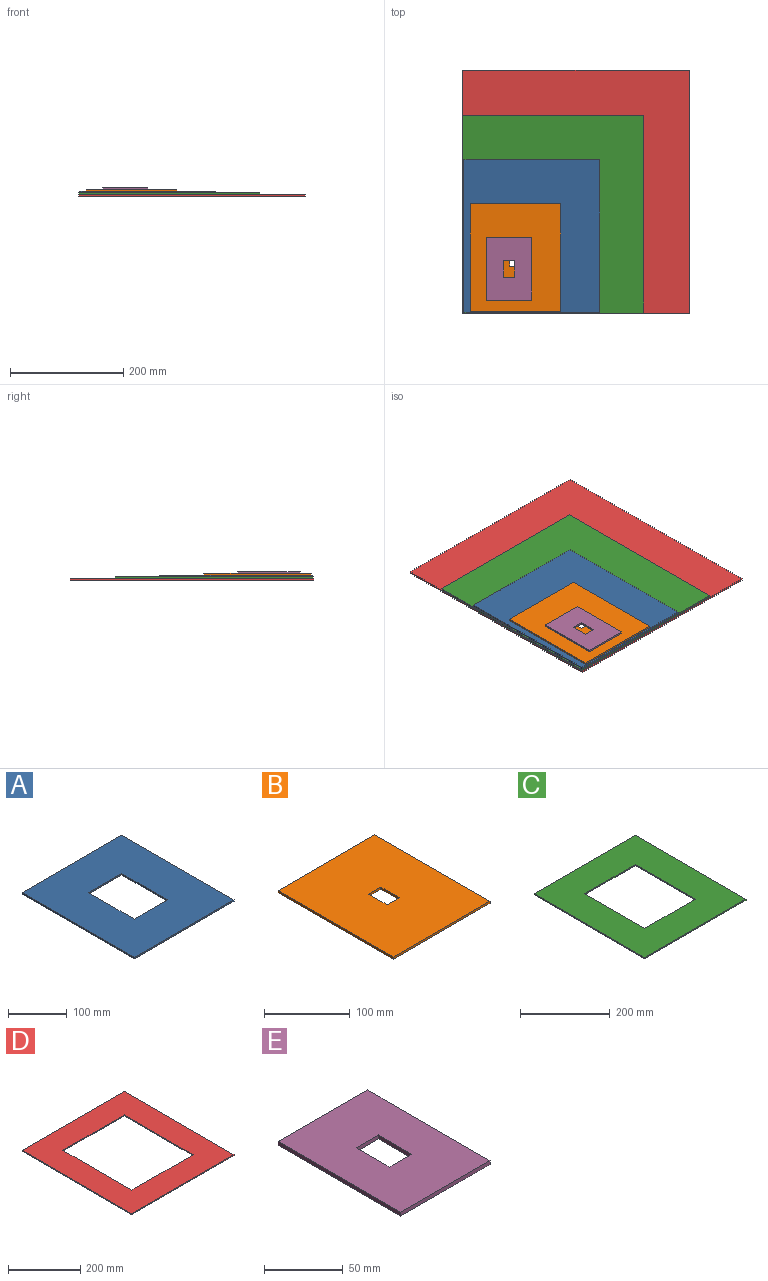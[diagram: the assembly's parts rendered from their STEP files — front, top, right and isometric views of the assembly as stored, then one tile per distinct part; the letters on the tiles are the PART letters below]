
ASSEMBLY  parts=5 mates=4
PART A: 10 faces, bbox 240x270x3 mm
  f0: plane 110x3mm, normal (1,0,0), area 330mm2, adj f1,f7,f8,f9
  f1: plane 80x3mm, normal (0,-1,0), area 240mm2, adj f0,f2,f8,f9
  f2: plane 110x3mm, normal (-1,0,0), area 330mm2, adj f1,f7,f8,f9
  f3: plane 270x3mm, normal (-1,0,0), area 810mm2, adj f4,f6,f8,f9
  f4: plane 240x3mm, normal (0,-1,0), area 720mm2, adj f3,f5,f8,f9
  f5: plane 270x3mm, normal (1,0,0), area 810mm2, adj f4,f6,f8,f9
  f6: plane 240x3mm, normal (0,1,0), area 720mm2, adj f3,f5,f8,f9
  f7: plane 80x3mm, normal (0,1,0), area 240mm2, adj f0,f2,f8,f9
  f8: plane 270x240mm, normal (0,0,1), area 56000mm2, adj f0,f1,f2,f3,f4,f5,f6,f7
  f9: plane 270x240mm, normal (0,0,-1), area 56000mm2, adj f0,f1,f2,f3,f4,f5,f6,f7
PART B: 10 faces, bbox 160x190x3 mm
  f0: plane 30x3mm, normal (1,0,0), area 90mm2, adj f1,f7,f8,f9
  f1: plane 20x3mm, normal (0,-1,0), area 60mm2, adj f0,f2,f8,f9
  f2: plane 30x3mm, normal (-1,0,0), area 90mm2, adj f1,f7,f8,f9
  f3: plane 160x3mm, normal (0,1,0), area 480mm2, adj f4,f6,f8,f9
  f4: plane 190x3mm, normal (-1,0,0), area 570mm2, adj f3,f5,f8,f9
  f5: plane 160x3mm, normal (0,-1,0), area 480mm2, adj f4,f6,f8,f9
  f6: plane 190x3mm, normal (1,0,0), area 570mm2, adj f3,f5,f8,f9
  f7: plane 20x3mm, normal (0,1,0), area 60mm2, adj f0,f2,f8,f9
  f8: plane 190x160mm, normal (0,0,1), area 29800mm2, adj f0,f1,f2,f3,f4,f5,f6,f7
  f9: plane 190x160mm, normal (0,0,-1), area 29800mm2, adj f0,f1,f2,f3,f4,f5,f6,f7
PART C: 10 faces, bbox 320x350x3 mm
  f0: plane 190x3mm, normal (1,0,0), area 570mm2, adj f1,f7,f8,f9
  f1: plane 160x3mm, normal (0,-1,0), area 480mm2, adj f0,f2,f8,f9
  f2: plane 190x3mm, normal (-1,0,0), area 570mm2, adj f1,f7,f8,f9
  f3: plane 350x3mm, normal (-1,0,0), area 1050mm2, adj f4,f6,f8,f9
  f4: plane 320x3mm, normal (0,-1,0), area 960mm2, adj f3,f5,f8,f9
  f5: plane 350x3mm, normal (1,0,0), area 1050mm2, adj f4,f6,f8,f9
  f6: plane 320x3mm, normal (0,1,0), area 960mm2, adj f3,f5,f8,f9
  f7: plane 160x3mm, normal (0,1,0), area 480mm2, adj f0,f2,f8,f9
  f8: plane 350x320mm, normal (0,0,1), area 81600mm2, adj f0,f1,f2,f3,f4,f5,f6,f7
  f9: plane 350x320mm, normal (0,0,-1), area 81600mm2, adj f0,f1,f2,f3,f4,f5,f6,f7
PART D: 10 faces, bbox 400x430x3 mm
  f0: plane 270x3mm, normal (-1,0,0), area 810mm2, adj f1,f7,f8,f9
  f1: plane 240x3mm, normal (0,1,0), area 720mm2, adj f0,f2,f8,f9
  f2: plane 270x3mm, normal (1,0,0), area 810mm2, adj f1,f7,f8,f9
  f3: plane 400x3mm, normal (0,1,0), area 1200mm2, adj f4,f6,f8,f9
  f4: plane 430x3mm, normal (-1,0,0), area 1290mm2, adj f3,f5,f8,f9
  f5: plane 400x3mm, normal (0,-1,0), area 1200mm2, adj f4,f6,f8,f9
  f6: plane 430x3mm, normal (1,0,0), area 1290mm2, adj f3,f5,f8,f9
  f7: plane 240x3mm, normal (0,-1,0), area 720mm2, adj f0,f2,f8,f9
  f8: plane 430x400mm, normal (0,0,1), area 107200mm2, adj f0,f1,f2,f3,f4,f5,f6,f7
  f9: plane 430x400mm, normal (0,0,-1), area 107200mm2, adj f0,f1,f2,f3,f4,f5,f6,f7
PART E: 10 faces, bbox 80x110x3 mm
  f0: plane 80x3mm, normal (0,1,0), area 240mm2, adj f1,f7,f8,f9
  f1: plane 110x3mm, normal (-1,0,0), area 330mm2, adj f0,f2,f8,f9
  f2: plane 80x3mm, normal (0,-1,0), area 240mm2, adj f1,f7,f8,f9
  f3: plane 30x3mm, normal (1,0,0), area 90mm2, adj f4,f6,f8,f9
  f4: plane 20x3mm, normal (0,-1,0), area 60mm2, adj f3,f5,f8,f9
  f5: plane 30x3mm, normal (-1,0,0), area 90mm2, adj f4,f6,f8,f9
  f6: plane 20x3mm, normal (0,1,0), area 60mm2, adj f3,f5,f8,f9
  f7: plane 110x3mm, normal (1,0,0), area 330mm2, adj f0,f2,f8,f9
  f8: plane 110x80mm, normal (0,0,1), area 8200mm2, adj f0,f1,f2,f3,f4,f5,f6,f7
  f9: plane 110x80mm, normal (0,0,-1), area 8200mm2, adj f0,f1,f2,f3,f4,f5,f6,f7
PLACE A t=(-78,-78,-229)mm
PLACE B t=(-107,-116,-226)mm
PLACE C t=(-40,-39,-232)mm
PLACE D t=(0,0,-235)mm
PLACE E t=(-118,-136,-223)mm
MATE planar E.f9 <-> B.f8  axis (0,0,-1) through (-118,-136,-223)mm
MATE planar B.f9 <-> A.f8  axis (0,0,-1) through (-107,-116,-226)mm
MATE planar C.f9 <-> D.f8  axis (0,0,-1) through (-40,-39,-232)mm
MATE planar A.f9 <-> C.f8  axis (0,0,-1) through (-78,-78,-229)mm
